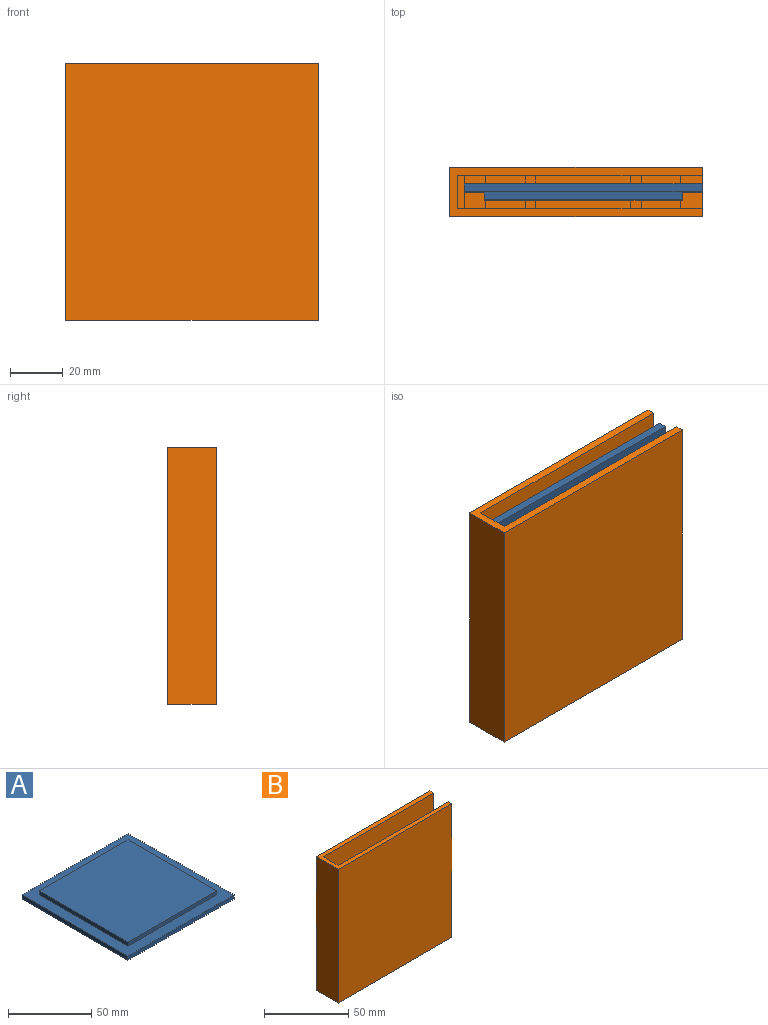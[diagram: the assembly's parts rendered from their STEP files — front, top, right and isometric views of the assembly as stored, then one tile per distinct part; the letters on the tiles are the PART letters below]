
ASSEMBLY  parts=2 mates=2
PART A: 11 faces, bbox 90x90x6 mm
  f0: plane 90x90mm, normal (0,0,1), area 2475mm2, adj f1,f2,f3,f4,f6,f7,f8,f9
  f1: plane 90x3mm, normal (1,0,0), area 270mm2, adj f0,f2,f4,f5
  f2: plane 90x3mm, normal (0,1,0), area 270mm2, adj f0,f1,f3,f5
  f3: plane 90x3mm, normal (-1,0,0), area 270mm2, adj f0,f2,f4,f5
  f4: plane 90x3mm, normal (0,-1,0), area 270mm2, adj f0,f1,f3,f5
  f5: plane 90x90mm, normal (0,0,-1), area 8100mm2, adj f1,f2,f3,f4
  f6: plane 75x3mm, normal (1,0,0), area 225mm2, adj f0,f7,f9,f10
  f7: plane 75x3mm, normal (0,1,0), area 225mm2, adj f0,f6,f8,f10
  f8: plane 75x3mm, normal (-1,0,0), area 225mm2, adj f0,f7,f9,f10
  f9: plane 75x3mm, normal (0,-1,0), area 225mm2, adj f0,f6,f8,f10
  f10: plane 75x75mm, normal (0,0,1), area 5625mm2, adj f6,f7,f8,f9
PART B: 36 faces, bbox 95.5x18.5x97 mm
  f0: plane 36x12.5mm, normal (0,0,1), area 450mm2, adj f1,f4,f18,f21
  f1: plane 95x92.5mm, normal (0,1,0), area 8635.5mm2, adj f0,f2,f3,f8,f9,f11,f12,f13
  f2: plane 15x12.5mm, normal (0,0,1), area 187.5mm2, adj f1,f4,f13,f20
  f3: plane 15x12.5mm, normal (0,0,1), area 187.5mm2, adj f1,f4,f15,f17
  f4: plane 95x92.5mm, normal (0,-1,0), area 8695.5mm2, adj f0,f2,f3,f8,f9,f11,f12,f13
  f5: plane 97x95.5mm, normal (0,1,0), area 9263.5mm2, adj f6,f9,f10,f35
  f6: plane 97x18.5mm, normal (-1,0,0), area 1794.5mm2, adj f5,f7,f9,f10
  f7: plane 97x95.5mm, normal (0,-1,0), area 9263.5mm2, adj f6,f9,f10,f35
  f8: plane 87x12.5mm, normal (1,0,0), area 1087.5mm2, adj f1,f4,f9,f12
  f9: plane 95.5x18.5mm, normal (0,0,1), area 610.5mm2, adj f1,f4,f5,f6,f7,f8,f35
  f10: plane 95.5x18.5mm, normal (0,0,-1), area 1766.7mm2, adj f5,f6,f7,f35
  f11: plane 12.5x6mm, normal (1,0,0), area 75mm2, adj f1,f4,f12,f16
  f12: plane 12.5x2.5mm, normal (0,0,1), area 31.3mm2, adj f1,f4,f8,f11
  f13: plane 12.5x2mm, normal (-1,0,0), area 25mm2, adj f1,f2,f4,f14
  f14: plane 12.5x8mm, normal (0,0,1), area 100mm2, adj f1,f4,f13,f35
  f15: plane 12.5x2mm, normal (1,0,0), area 25mm2, adj f1,f3,f4,f16
  f16: plane 12.5x8mm, normal (0,0,1), area 100mm2, adj f1,f4,f11,f15
  f17: plane 12.5x12.5mm, normal (-1,0,0), area 91.4mm2, adj f1,f3,f4,f19,f25,f26,f27,f28
  f18: plane 12.5x12.5mm, normal (1,0,0), area 91.4mm2, adj f0,f1,f4,f19,f25,f26,f27,f28
  f19: plane 4x3mm, normal (0,0,1), area 12mm2, adj f17,f18,f25,f27
  f20: plane 12.5x12.5mm, normal (1,0,0), area 91.4mm2, adj f1,f2,f4,f22,f23,f24,f29,f30
  f21: plane 12.5x12.5mm, normal (-1,0,0), area 91.4mm2, adj f0,f1,f4,f22,f23,f24,f29,f30
  f22: plane 4x3mm, normal (0,0,1), area 12mm2, adj f20,f21,f23,f29
  f23: plane 4x3mm, normal (0,-1,0), area 12mm2, adj f20,f21,f22,f24
  f24: plane 4x3.25mm, normal (0,0,1), area 13mm2, adj f4,f20,f21,f23
  f25: plane 4x3mm, normal (0,-1,0), area 12mm2, adj f17,f18,f19,f26
  f26: plane 4x3.25mm, normal (0,0,1), area 13mm2, adj f4,f17,f18,f25
  f27: plane 7.5x4mm, normal (0,1,0), area 30mm2, adj f17,f18,f19,f28
  f28: plane 4x3mm, normal (0,0,1), area 12mm2, adj f17,f18,f27,f33
  f29: plane 7.5x4mm, normal (0,1,0), area 30mm2, adj f20,f21,f22,f30
  f30: plane 4x3mm, normal (0,0,1), area 12mm2, adj f20,f21,f29,f31
  f31: plane 4x3mm, normal (0,1,0), area 12mm2, adj f20,f21,f30,f32
  f32: plane 4x3.25mm, normal (0,0,1), area 13mm2, adj f1,f20,f21,f31
  f33: plane 4x3mm, normal (0,1,0), area 12mm2, adj f17,f18,f28,f34
  f34: plane 4x3.25mm, normal (0,0,1), area 13mm2, adj f1,f17,f18,f33
  f35: plane 97x18.5mm, normal (1,0,0), area 632mm2, adj f1,f4,f5,f7,f9,f10,f14
PLACE A rot(axis=(1,0,0),90deg) t=(0,3,-0.5)mm
PLACE B at identity fixed
MATE planar A.f5 <-> B.f25  axis (0,1,0) through (0,3,-0.5)mm
MATE planar A.f4 <-> B.f19  axis (0,0,-1) through (0,1.5,-45.5)mm
